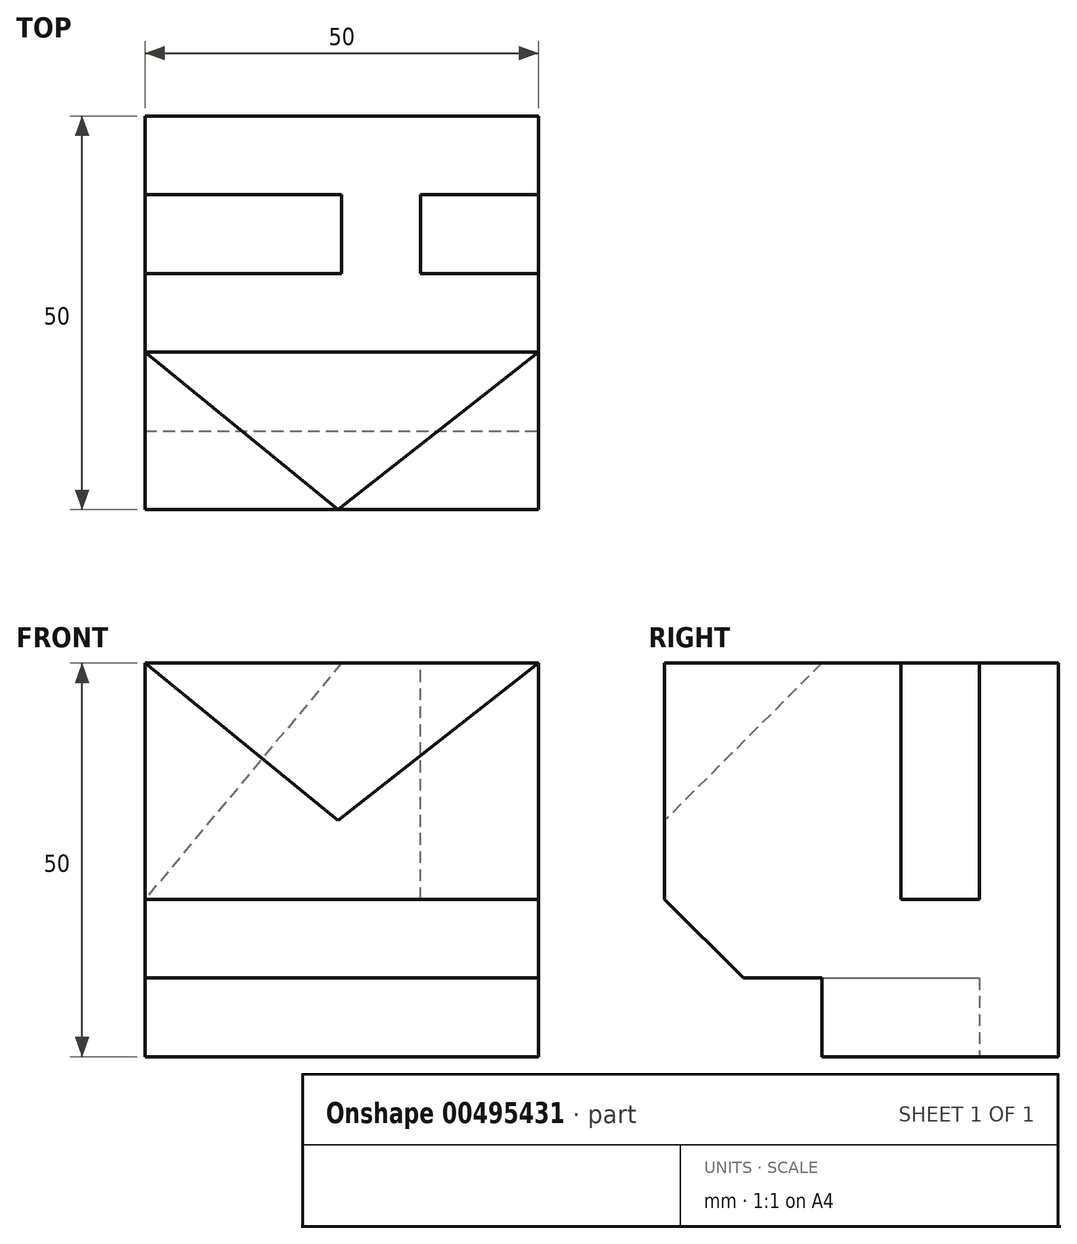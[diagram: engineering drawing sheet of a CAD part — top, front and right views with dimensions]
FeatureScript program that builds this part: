
annotation { "Feature Type Name" : "Feature", "Feature Type Description" : "" }
export const myFeature = defineFeature(function(context is Context, id is Id, definition is map)
    precondition{}
    {
        {
            var Q0;
            Q0=qCreatedBy(makeId("Front.planeOp"),FACE);
            var sketch = newSketch(context, id + "F0", { "sketchPlane" : qUnion([Q0])});
            skLineSegment(sketch, "E0.bottom", {"start": v(0, 0) * mm, "end": v(-50, 0) * mm});
            skLineSegment(sketch, "E0.top", {"start": v(0, 50) * mm, "end": v(-50, 50) * mm});
            skLineSegment(sketch, "E0.left", {"start": v(0, 0) * mm, "end": v(0, 50) * mm});
            skLineSegment(sketch, "E0.right", {"start": v(-50, 0) * mm, "end": v(-50, 50) * mm});
            skSolve(sketch);
        }
        {
            var Q0;
            Q0=makeQuery(id+"F0.imprint","IMPRINT",FACE,{"disambiguationData":[TD([[makeQuery(id+"F0.imprint","IMPRINT",EDGE,{"derivedFrom":sQuery(id+"F0.wireOp",EDGE,"E0.bottom")}),-1.0]])]});
            extrude(context, id + "F1", {"entities" : qUnion([Q0]), "depth" : 50 * mm});
        }
        {
            var Q0;
            Q0=makeQuery(id+"F1.opExtrude","SWEPT_FACE",FACE,{"disambiguationData":[OSD([sQuery(id+"F0.wireOp",EDGE,"E0.bottom")])]});
            var sketch = newSketch(context, id + "F2", { "sketchPlane" : qUnion([Q0])});
            skLineSegment(sketch, "E1", {"start": v(0, 50) * mm, "end": v(0, 30) * mm});
            skLineSegment(sketch, "E2", {"start": v(0, 30) * mm, "end": v(-50, 10) * mm});
            skLineSegment(sketch, "E3", {"start": v(-50, 10) * mm, "end": v(-50, 30) * mm});
            skLineSegment(sketch, "E4", {"start": v(-50, 30) * mm, "end": v(0, 50) * mm});
            skSolve(sketch);
        }
        {
            var Q0;
            Q0=makeQuery(id+"F2.imprint","IMPRINT",FACE,{"disambiguationData":[TD([[makeQuery(id+"F2.imprint","IMPRINT",EDGE,{"derivedFrom":sQuery(id+"F2.wireOp",EDGE,"E1")}),-1.0]])]});
            extrude(context, id + "F3", {"entities" : qUnion([Q0]), "operationType" : NewBodyOperationType.REMOVE, "oppositeDirection" : true, "depth" : 10 * mm});
        }
        {
            var Q0;
            Q0=makeQuery(id+"F1.opExtrude","SWEPT_FACE",FACE,{"disambiguationData":[OSD([sQuery(id+"F0.wireOp",EDGE,"E0.right")])]});
            var sketch = newSketch(context, id + "F4", { "sketchPlane" : qUnion([Q0])});
            skLineSegment(sketch, "E5.bottom", {"start": v(30, 0) * mm, "end": v(50, 0) * mm});
            skLineSegment(sketch, "E5.top", {"start": v(30, 10) * mm, "end": v(50, 10) * mm});
            skLineSegment(sketch, "E5.left", {"start": v(30, 0) * mm, "end": v(30, 10) * mm});
            skLineSegment(sketch, "E5.right", {"start": v(50, 0) * mm, "end": v(50, 10) * mm});
            skSolve(sketch);
        }
        {
            var Q0;
            Q0=makeQuery(id+"F4.imprint","IMPRINT",FACE,{"disambiguationData":[TD([[makeQuery(id+"F4.imprint","IMPRINT",EDGE,{"derivedFrom":sQuery(id+"F4.wireOp",EDGE,"E5.bottom")}),-1.0]])]});
            extrude(context, id + "F5", {"entities" : qUnion([Q0]), "operationType" : NewBodyOperationType.REMOVE, "endBound" : BoundingType.THROUGH_ALL, "oppositeDirection" : true, "depth" : 25 * mm});
        }
        {
            var Q0;
            Q0=makeQuery(id+"F1.opExtrude","SWEPT_FACE",FACE,{"disambiguationData":[OSD([sQuery(id+"F0.wireOp",EDGE,"E0.left")])]});
            var sketch = newSketch(context, id + "F6", { "sketchPlane" : qUnion([Q0])});
            skLineSegment(sketch, "E6", {"start": v(-50, 10) * mm, "end": v(-50, 20) * mm});
            skLineSegment(sketch, "E7", {"start": v(-50, 20) * mm, "end": v(-40, 10) * mm});
            skLineSegment(sketch, "E8", {"start": v(-40, 10) * mm, "end": v(-50, 10) * mm});
            skSolve(sketch);
        }
        {
            var Q0;
            Q0=makeQuery(id+"F6.imprint","IMPRINT",FACE,{"disambiguationData":[TD([[makeQuery(id+"F6.imprint","IMPRINT",EDGE,{"derivedFrom":sQuery(id+"F6.wireOp",EDGE,"E6")}),-1.0]])]});
            extrude(context, id + "F7", {"entities" : qUnion([Q0]), "operationType" : NewBodyOperationType.REMOVE, "endBound" : BoundingType.THROUGH_ALL, "oppositeDirection" : true, "depth" : 25 * mm});
        }
        {
            var Q0;
            Q0=makeQuery(id+"F1.opExtrude","SWEPT_FACE",FACE,{"disambiguationData":[OSD([sQuery(id+"F0.wireOp",EDGE,"E0.top")])]});
            var sketch = newSketch(context, id + "F8", { "sketchPlane" : qUnion([Q0])});
            skLineSegment(sketch, "E9.bottom", {"start": v(0, -10) * mm, "end": v(-15, -10) * mm});
            skLineSegment(sketch, "E9.top", {"start": v(0, -20) * mm, "end": v(-15, -20) * mm});
            skLineSegment(sketch, "E9.left", {"start": v(0, -10) * mm, "end": v(0, -20) * mm});
            skLineSegment(sketch, "E9.right", {"start": v(-15, -10) * mm, "end": v(-15, -20) * mm});
            skSolve(sketch);
        }
        {
            var Q0;
            Q0=makeQuery(id+"F8.imprint","IMPRINT",FACE,{"disambiguationData":[TD([[makeQuery(id+"F8.imprint","IMPRINT",EDGE,{"derivedFrom":sQuery(id+"F8.wireOp",EDGE,"E9.bottom")}),1.0]])]});
            extrude(context, id + "F9", {"entities" : qUnion([Q0]), "operationType" : NewBodyOperationType.REMOVE, "oppositeDirection" : true, "depth" : 30 * mm});
        }
        {
            var Q0;
            Q0=makeQuery(id+"F1.opExtrude","CAP_FACE",FACE,{"disambiguationData":[OSD([sQuery(id+"F0.wireOp",EDGE,"E0.bottom"),sQuery(id+"F0.wireOp",EDGE,"E0.top"),sQuery(id+"F0.wireOp",EDGE,"E0.left"),sQuery(id+"F0.wireOp",EDGE,"E0.right")])],"isStart":true});
            cPlane(context, id + "F10", {"entities" : qUnion([Q0]), "cplaneType" : CPlaneType.OFFSET, "offset" : 10 * mm, "oppositeDirection" : true, "width" : 150 * mm, "height" : 150 * mm});
        }
        {
            var Q0;
            Q0=makeQuery(id+"F1.opExtrude","SWEPT_FACE",FACE,{"disambiguationData":[OSD([sQuery(id+"F0.wireOp",EDGE,"E0.top")])]});
            var sketch = newSketch(context, id + "F11", { "sketchPlane" : qUnion([Q0])});
            skLineSegment(sketch, "E10.bottom", {"start": v(-50, -10) * mm, "end": v(-25, -10) * mm});
            skLineSegment(sketch, "E10.top", {"start": v(-50, -20) * mm, "end": v(-25, -20) * mm});
            skLineSegment(sketch, "E10.left", {"start": v(-50, -10) * mm, "end": v(-50, -20) * mm});
            skLineSegment(sketch, "E10.right", {"start": v(-25, -10) * mm, "end": v(-25, -20) * mm});
            skSolve(sketch);
        }
        {
            var Q0;
            Q0=makeQuery(id+"F1.opExtrude","SWEPT_FACE",FACE,{"disambiguationData":[OSD([sQuery(id+"F0.wireOp",EDGE,"E0.right")])]});
            var sketch = newSketch(context, id + "F12", { "sketchPlane" : qUnion([Q0])});
            skLineSegment(sketch, "E11.bottom", {"start": v(10, 50) * mm, "end": v(20, 50) * mm});
            skLineSegment(sketch, "E11.top", {"start": v(10, 20) * mm, "end": v(20, 20) * mm});
            skLineSegment(sketch, "E11.left", {"start": v(10, 50) * mm, "end": v(10, 20) * mm});
            skLineSegment(sketch, "E11.right", {"start": v(20, 50) * mm, "end": v(20, 20) * mm});
            skSolve(sketch);
        }
        {
            var Q0;
            Q0=qCreatedBy(id+"F10.planeOp",FACE);
            var sketch = newSketch(context, id + "F13", { "sketchPlane" : qUnion([Q0])});
            skLineSegment(sketch, "E12", {"start": v(25, 50) * mm, "end": v(50, 20) * mm});
            skSolve(sketch);
        }
        {
            var Q0;
            Q0=makeQuery(id+"F11.imprint","IMPRINT",FACE,{"disambiguationData":[TD([[makeQuery(id+"F11.imprint","IMPRINT",EDGE,{"derivedFrom":sQuery(id+"F11.wireOp",EDGE,"E10.bottom")}),-1.0]])]});
            var Q1;
            Q1=sQuery(id+"F13.wireOp",EDGE,"E12");
            sweep(context, id + "F14", {"operationType" : NewBodyOperationType.REMOVE, "profiles" : qUnion([Q0]), "path" : qUnion([Q1])});
        }
        {
            var Q0;
            Q0=makeQuery(id+"F1.opExtrude","SWEPT_FACE",FACE,{"disambiguationData":[OSD([sQuery(id+"F0.wireOp",EDGE,"E0.top")])]});
            var sketch = newSketch(context, id + "F15", { "sketchPlane" : qUnion([Q0])});
            skLineSegment(sketch, "E13.bottom", {"start": v(-50, -50) * mm, "end": v(0, -50) * mm});
            skLineSegment(sketch, "E13.top", {"start": v(-50, -30) * mm, "end": v(0, -30) * mm});
            skLineSegment(sketch, "E13.left", {"start": v(-50, -50) * mm, "end": v(-50, -30) * mm});
            skLineSegment(sketch, "E13.right", {"start": v(0, -50) * mm, "end": v(0, -30) * mm});
            skSolve(sketch);
        }
        {
            var Q0;
            Q0=makeQuery(id+"F1.opExtrude","SWEPT_FACE",FACE,{"disambiguationData":[OSD([sQuery(id+"F0.wireOp",EDGE,"E0.left")])]});
            cPlane(context, id + "F16", {"entities" : qUnion([Q0]), "cplaneType" : CPlaneType.OFFSET, "offset" : 25 * mm, "oppositeDirection" : true, "width" : 150 * mm, "height" : 150 * mm});
        }
        {
            var Q0;
            Q0=qCreatedBy(id+"F16.planeOp",FACE);
            var sketch = newSketch(context, id + "F17", { "sketchPlane" : qUnion([Q0])});
            skLineSegment(sketch, "E14", {"start": v(-50, 30) * mm, "end": v(-30, 50) * mm});
            skSolve(sketch);
        }
        {
            var Q0;
            Q0=sQuery(id+"F15.wireOp",VERTEX,"E13.left.end");
            var Q1;
            Q1=sQuery(id+"F15.wireOp",VERTEX,"E13.right.end");
            var Q2;
            Q2=sQuery(id+"F17.wireOp",VERTEX,"E14.start");
            cPlane(context, id + "F18", {"entities" : qUnion([Q0, Q1, Q2]), "cplaneType" : CPlaneType.THREE_POINT, "offset" : 25 * mm, "width" : 150 * mm, "height" : 150 * mm});
        }
        {
            var Q0;
            Q0=makeQuery(id+"F1.opExtrude","CAP_FACE",FACE,{"disambiguationData":[OSD([sQuery(id+"F0.wireOp",EDGE,"E0.bottom"),sQuery(id+"F0.wireOp",EDGE,"E0.top"),sQuery(id+"F0.wireOp",EDGE,"E0.left"),sQuery(id+"F0.wireOp",EDGE,"E0.right")])],"isStart":false});
            var sketch = newSketch(context, id + "F19", { "sketchPlane" : qUnion([Q0])});
            skLineSegment(sketch, "E15", {"start": v(-50, 50) * mm, "end": v(0, 50) * mm});
            skLineSegment(sketch, "E16", {"start": v(0, 50) * mm, "end": v(-25.5, 30) * mm});
            skLineSegment(sketch, "E17", {"start": v(-25.5, 30) * mm, "end": v(-50, 50) * mm});
            skSolve(sketch);
        }
        {
            var Q0;
            Q0=makeQuery(id+"F19.imprint","IMPRINT",FACE,{"disambiguationData":[TD([[makeQuery(id+"F19.imprint","IMPRINT",EDGE,{"derivedFrom":sQuery(id+"F19.wireOp",EDGE,"E15")}),1.0]])]});
            var Q1;
            Q1=qCreatedBy(id+"F18.planeOp",FACE);
            extrude(context, id + "F20", {"entities" : qUnion([Q0]), "operationType" : NewBodyOperationType.REMOVE, "endBound" : BoundingType.UP_TO_SURFACE, "oppositeDirection" : true, "endBoundEntityFace" : qUnion([Q1]), "depth" : 25 * mm});
        }
    });
